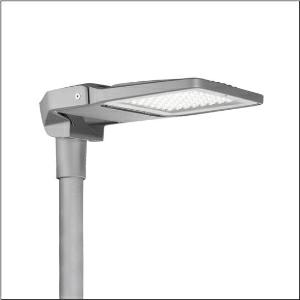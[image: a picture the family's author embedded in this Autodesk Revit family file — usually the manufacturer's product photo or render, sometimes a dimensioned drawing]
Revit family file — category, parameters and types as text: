
# Revit family: floodlight_fl_20_mini___pl61_5xa7672c2c4ac_8a85
name_source: partatom
category: Lighting Fixtures
units: mm (PartAtom-declared; Revit-internal decimal feet)

## family parameters
Cut with Voids When Loaded = No
Host = Face
Light Source = No
Part Type = Normal
Room Calculation Point = No
Round Connector Dimension = Use Diameter
Shared = No

## types (1)
- --- (1 x LED 4000K / CRI = 70 (unbekannt), 12430 lm, 4000K)
    Apparent Load = 96 VA
    CIE Flux Codes = 33 65 98 100 100
    Color Rendering = 70
    Color Temperature = 4000K
    Default Elevation = 1800 mm
    Description = Floodlight FL 20 mini, floodlight, primary light control with lens, of plastic, primary optical cover: protective disc, of toughened safety glass, transparent, light distribution: PL61, light emission: direct distribution, primary light characteristic: asymmetric, installation type: side-entry, post-top, LED, High Power LED, rated luminous flux: 12.430lm, luminous efficacy: 130lm/W, light colour: 740, colour temperature: 4000K, control gear: ECG Plus, control: flexible luminous flux parameterisation, time-dependent luminous flux control, digital communication interface, overheat protection, power reduction, electronic power reduction, with terminal, 5-pole, max. 2.5mm², mains connection: 220..240V, AC, 50/60Hz, rated input power: 96W, LED unit, of diecast aluminium, powder-coated, Siteco® metallic grey (DB 702S), corrosivity category C5 mid according to DIN EN ISO 12944, incl. 1x M20 cable gland for cable Ø 6.5..12mm, inclination adjustable: 0°, 5°, 10°, 15°, please order mast flange separately, length: 565mm, width: 335mm, height: 119mm, housing frame, of diecast aluminium, powder-coated, Siteco® metallic grey (DB 702S), mast flange adapter, of diecast aluminium, powder-coated, Siteco® metallic grey (DB 702S), DALI, protection rating (complete): IP66, insulation class (complete): insulation class II (safety insulation), certification: CE, ENEC, VDE, protection symbol: D, permissible operating ambient temperature: -40..+40°C, permissible operating ambient temperature for outdoor applications: -40..+50°C, standard: DIN EN 12944, packaging unit: 1 piece

Light Distribution: PL61
    Height = 62 mm  [stored 0.203412 ft]
    Lamp = 1 x LED 4000K / CRI >= 70 (unbekannt)
    Lamp Light Flux = 12430 lm
    Lamp count = 1
    Length = 565 mm
    Luminous efficacy = 130 lm/W
    Manufacturer = Siteco
    ModVariant = No
    Model = 5XA7672C2C4AC
    Number of Poles = 1
    OnlyDefault = Yes
    Power Factor = 1
    Product Name = Floodlight FL 20 mini | PL61
    Product group = floodlight | pylon top
    ProductGroupID = 6101
    Protection Class = Protection class II
    Protection Degree = IP 66
    RLX_Detail_Level = 1
    RLX_Emergency_Light_Flux = 0 lm
    RLX_Emergency_Type = 0
    RLX_Emergency_Type_DB = No
    RlxData = <blob elided: 102129 chars, md5=5a584709>
    Socket = socket
    Standby Power = 0 W
    System Light Flux = 12430 lm
    System Power = 96 W
    Type Comments = factory setting: luminous flux: 100 % | dim-lin: 254 | 500 mA
    Type Image = l_1005946.jpg
    URL = http://relux.com
    VarID = @adj_163161
    Voltage = 0 V
    Weight = 0.00 kg
    Width = 335 mm

note: [stored X ft] marks values corroborated as IEEE doubles in the binary element streams (Revit-internal decimal feet)

## geometry (parser evidence)
native form markers: Blend x4, Sweep x12
no freeform markers — native parametric forms only
